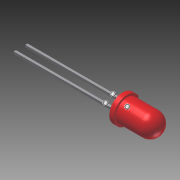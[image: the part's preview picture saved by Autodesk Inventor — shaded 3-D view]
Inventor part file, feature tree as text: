
AUTODESK INVENTOR PART (.ipt)
format: ipt  version: 2012 SP1 (Build 160190100, 190)  size: 176,640 bytes
history: native  units: mm
features: other x99, sketch x4, extrude x2, revolve x1, projected_geometry x1
ambient origin geometry x8: Origin, YZ Plane, XZ Plane, XY Plane, X Axis, Y Axis, Z Axis, Center Point
bodies: Solid1 (feature_tree)
feature tree (107):
  other  "Table"
  other  "LED Heigth mm 1.0"
  other  "LED Heigth mm 1.2"
  other  "LED Heigth mm 1.4"
  other  "LED Heigth mm 1.6"
  other  "LED Heigth mm 1.8"
  other  "LED Heigth mm 2.0"
  other  "LED Heigth mm 2.2"
  other  "LED Heigth mm 2.4"
  other  "LED Heigth mm 2.6"
  other  "LED  Heigth mm 2.8"
  other  "LED Heigth mm 3.0"
  other  "LED Heigth mm 3.2"
  other  "LED Heigth mm 3.4"
  other  "LED Heigth mm 3.6"
  other  "LED Heigth mm 3.8"
  other  "LED Heigth mm 4.0"
  other  "LED Heigth mm 4.2"
  other  "LED Heigth mm 4.4"
  other  "LED Heigth mm 4.6"
  other  "LED Heigth mm 4.8"
  other  "LED Heigth mm 5.0"
  other  "LED Heigth mm 5.2"
  other  "LED Heigth mm 5.4"
  other  "LED Heigth mm 5.6"
  other  "LED Heigth mm 5.8"
  other  "LED Heigth mm 6.0"
  other  "LED Heigth mm 6.2"
  other  "LED Heigth mm 6.4"
  other  "LED Heigth mm 6.6"
  other  "LED Heigth mm 6.8"
  other  "LED Heigth mm 7.0"
  other  "LED Heigth mm 7.2"
  other  "LED Heigth mm 7.4"
  other  "LED Heigth mm 7.6"
  other  "LED Heigth mm 7.8"
  other  "LED Heigth mm 8.0"
  other  "LED Heigth mm 8.2"
  other  "LED Heigth mm 8.4"
  other  "LED Heigth mm 8.6"
  other  "LED Heigth mm 8.8"
  other  "LED Heigth mm 9.0"
  other  "LED Heigth mm 9.2"
  other  "LED Heigth mm 9.4"
  other  "LED Heigth mm 9.6"
  other  "LED Heigth mm 9.8"
  other  "LED Heigth mm 10.0"
  other  "LED Heigth mm 10.2"
  other  "LED Heigth mm 10.4"
  other  "LED Heigth mm 10.6"
  other  "LED Heigth mm 10.8"
  other  "LED Heigth mm 11.0"
  other  "LED Heigth mm 11.2"
  other  "LED Heigth mm 11.4"
  other  "LED Heigth mm 11.6"
  other  "LED Heigth mm 11.8"
  other  "LED Heigth mm 12.0"
  other  "LED Heigth mm 12.2"
  other  "LED Heigth mm 12.4"
  other  "LED Heigth mm 12.6"
  other  "LED Heigth mm 12.8"
  other  "LED Heigth mm 13.0"
  other  "LED Heigth mm 13.2"
  other  "LED Heigth mm 13.4"
  other  "LED Heigth mm 13.6"
  other  "LED Heigth mm 13.8"
  other  "LED Heigth mm 14.0"
  other  "LED Heigth mm 14.2"
  other  "LED Heigth mm 14.4"
  other  "LED Heigth mm 14.6"
  other  "LED Heigth mm 14.8"
  other  "LED Heigth mm 15.0"
  other  "LED Heigth mm 15.2"
  other  "LED Heigth mm 15.4"
  other  "LED Heigth mm 15.6"
  other  "LED Heigth mm 15.8"
  other  "LED Heigth mm 16.0"
  other  "LED Heigth mm 16.2"
  other  "LED Heigth mm 16.4"
  other  "LED Heigth mm 16.6"
  other  "LED Heigth mm 16.8"
  other  "LED Heigth mm 17.0"
  other  "LED Heigth mm 17.2"
  other  "LED Heigth mm 17.4"
  other  "LED Heigth mm 17.6"
  other  "LED Heigth mm 17.8"
  other  "LED Heigth mm 18.0"
  other  "LED Heigth mm 18.2"
  other  "LED Heigth mm 18.4"
  other  "LED Heigth mm 18.6"
  other  "LED Heigth mm 18.8"
  other  "LED Heigth mm 19.0"
  other  "LED Heigth mm 19.2"
  other  "LED Heigth mm 19.4"
  other  "LED Heigth mm 19.6"
  other  "LED Heigth mm 19.8"
  other  "LED Heigth mm 20.0"
  revolve  "Revolution1"  [1 undecoded]
  extrude  "Extrusion1"  Depth=8.6mm
  extrude  "Extrusion2"  TaperAngle=90.0deg  [1 undecoded]
  sketch  "Sketch3"  dims[d5=2.5mm d6=90.0deg]
  other  "Work Axis1"
  other  "Work Axis2"
  sketch  "Sketch1"  dims[d1=2.95mm d2=1.0mm]
  sketch  "Sketch2"  dims[d3=5.0mm d4=8.6mm]
  projected_geometry  "Projected Loop1"
  sketch  "Sketch4"  dims[d7=0.5mm d8=0.5mm d9=1.27mm d10=1.27mm d12=0.0mm d13=20.0mm d14=0.0mm d15=0.0mm d16=10.0mm d17=0.0mm]
note: 2 required parameter values undecoded (feature->parameter linkage not recoverable at this tier; creation-order binding heuristic only, values carry confidence <= 0.55)